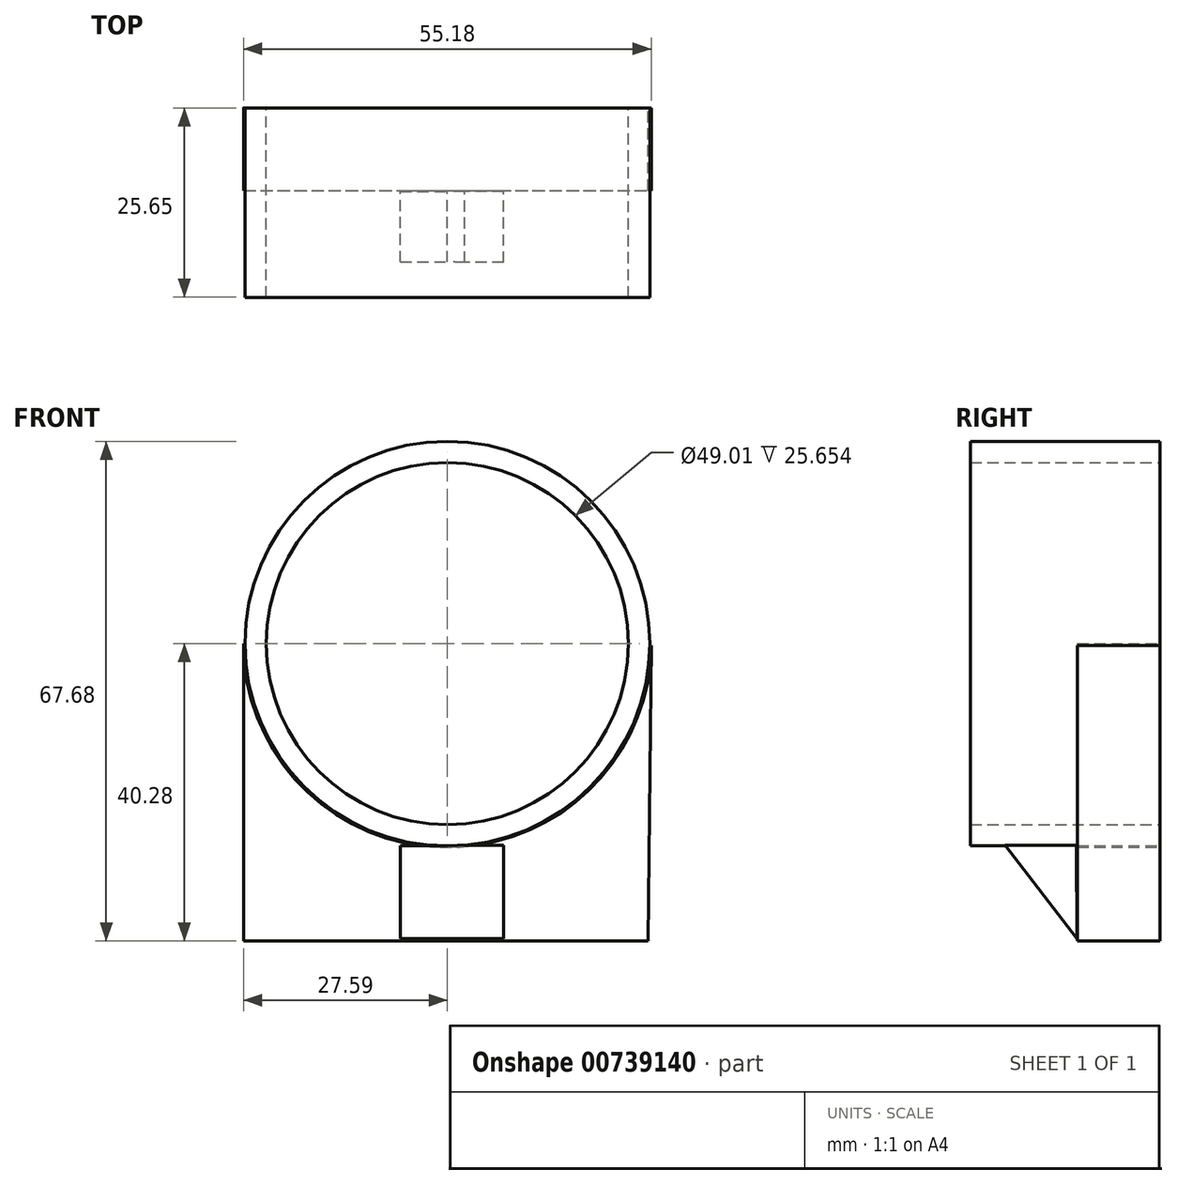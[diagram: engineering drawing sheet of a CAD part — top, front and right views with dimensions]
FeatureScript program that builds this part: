
annotation { "Feature Type Name" : "Feature", "Feature Type Description" : "" }
export const myFeature = defineFeature(function(context is Context, id is Id, definition is map)
    precondition{}
    {
        {
            var Q0;
            Q0=qCreatedBy(makeId("Front.planeOp"),FACE);
            var sketch = newSketch(context, id + "F0", { "sketchPlane" : qUnion([Q0])});
            skCircle(sketch, "E0", {"center": v(0, 0) * mm, "radius": 27.59 * mm});
            skLineSegment(sketch, "E1", {"start": v(-27.59, 0) * mm, "end": v(-27.59, -40.28) * mm});
            skLineSegment(sketch, "E2", {"start": v(-27.59, -40.28) * mm, "end": v(27.2, -40.28) * mm});
            skLineSegment(sketch, "E3", {"start": v(27.2, -40.28) * mm, "end": v(27.59, 0) * mm});
            skSolve(sketch);
        }
        {
            var Q0;
            {var subQ0=sQuery(id+"F0.wireOp",EDGE,"E1");Q0=makeQuery(id+"F0.imprint","IMPRINT",FACE,{"disambiguationData":[TD([[makeQuery(id+"F0.imprint","IMPRINT",EDGE,{"derivedFrom":subQ0}),1.0]])]});}
            extrude(context, id + "F1", {"entities" : qUnion([Q0]), "depth" : 11.18 * mm, "offsetDistance" : 25.4 * mm});
        }
        {
            var Q0;
            Q0=qCreatedBy(makeId("Front.planeOp"),FACE);
            var sketch = newSketch(context, id + "F2", { "sketchPlane" : qUnion([Q0])});
            skCircle(sketch, "E4", {"center": v(0, 0) * mm, "radius": 27.4 * mm});
            skCircle(sketch, "E5", {"center": v(0, 0) * mm, "radius": 24.5 * mm});
            skSolve(sketch);
        }
        {
            var Q0;
            Q0=makeQuery(id+"F2.imprint","IMPRINT",FACE,{"disambiguationData":[TD([[makeQuery(id+"F2.imprint","IMPRINT",EDGE,{"derivedFrom":sQuery(id+"F2.wireOp",EDGE,"E4")}),1.0]])]});
            extrude(context, id + "F3", {"entities" : qUnion([Q0]), "depth" : 25.65 * mm, "offsetDistance" : 25.4 * mm});
        }
        {
            var Q0;
            Q0=qCreatedBy(makeId("Right.planeOp"),FACE);
            var sketch = newSketch(context, id + "F4", { "sketchPlane" : qUnion([Q0])});
            skLineSegment(sketch, "E6", {"start": v(-20.95, -27.3) * mm, "end": v(-11.26, -39.93) * mm});
            skLineSegment(sketch, "E7", {"start": v(-20.95, -27.3) * mm, "end": v(-11.34, -27.3) * mm});
            skLineSegment(sketch, "E8", {"start": v(-11.34, -27.3) * mm, "end": v(-11.26, -39.93) * mm});
            skSolve(sketch);
        }
        {
            var Q0;
            Q0=makeQuery(id+"F4.imprint","IMPRINT",FACE,{"disambiguationData":[TD([[makeQuery(id+"F4.imprint","IMPRINT",EDGE,{"derivedFrom":sQuery(id+"F4.wireOp",EDGE,"E6")}),1.0]])]});
            extrude(context, id + "F5", {"entities" : qUnion([Q0]), "operationType" : NewBodyOperationType.ADD, "depth" : 7.62 * mm, "offsetDistance" : 25.4 * mm});
        }
        {
            var Q0;
            Q0=makeQuery(id+"F5.opExtrude","CAP_FACE",FACE,{"disambiguationData":[OSD([sQuery(id+"F4.wireOp",EDGE,"E6"),sQuery(id+"F4.wireOp",EDGE,"E7"),sQuery(id+"F4.wireOp",EDGE,"E8")])],"isStart":true});
            extrude(context, id + "F6", {"entities" : qUnion([Q0]), "operationType" : NewBodyOperationType.ADD, "depth" : 6.35 * mm, "offsetDistance" : 25.4 * mm});
        }
    });
